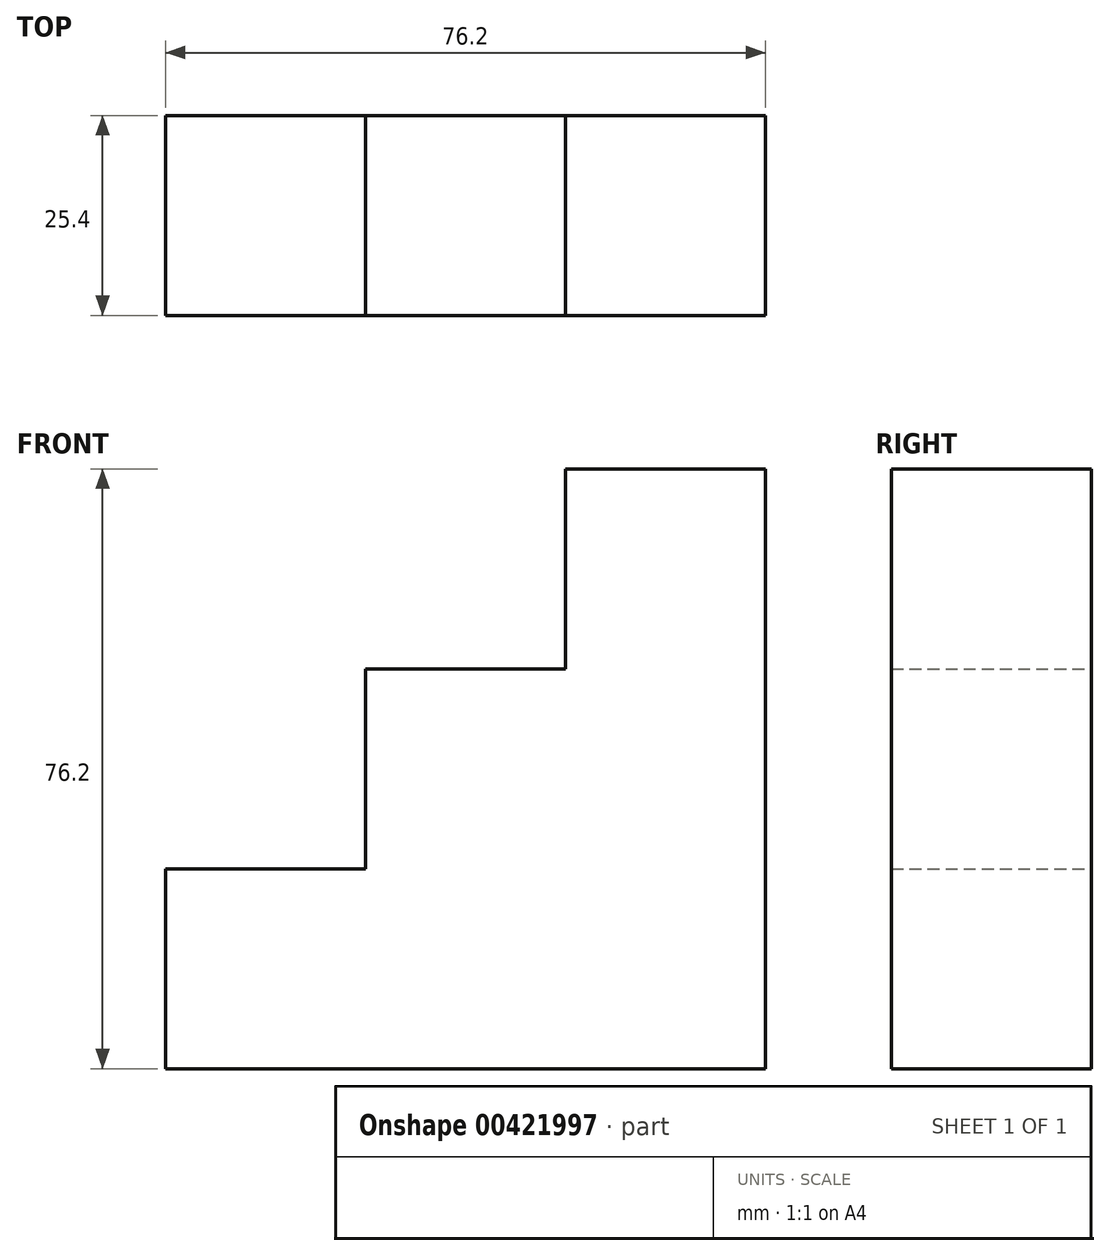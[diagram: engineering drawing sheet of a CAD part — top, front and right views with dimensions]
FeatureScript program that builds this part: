
annotation { "Feature Type Name" : "Feature", "Feature Type Description" : "" }
export const myFeature = defineFeature(function(context is Context, id is Id, definition is map)
    precondition{}
    {
        {
            var Q0;
            Q0=qCreatedBy(makeId("Front.planeOp"),FACE);
            var sketch = newSketch(context, id + "F0", { "sketchPlane" : qUnion([Q0])});
            skLineSegment(sketch, "E0", {"start": v(0, 0) * mm, "end": v(-76.2, 0) * mm});
            skLineSegment(sketch, "E1", {"start": v(-76.2, 0) * mm, "end": v(-76.2, 25.4) * mm});
            skLineSegment(sketch, "E2", {"start": v(-76.2, 25.4) * mm, "end": v(-50.8, 25.4) * mm});
            skLineSegment(sketch, "E3", {"start": v(-50.8, 25.4) * mm, "end": v(-50.8, 50.8) * mm});
            skLineSegment(sketch, "E4", {"start": v(-50.8, 50.8) * mm, "end": v(-25.4, 50.8) * mm});
            skLineSegment(sketch, "E5", {"start": v(-25.4, 50.8) * mm, "end": v(-25.4, 76.2) * mm});
            skLineSegment(sketch, "E6", {"start": v(-25.4, 76.2) * mm, "end": v(0, 76.2) * mm});
            skLineSegment(sketch, "E7", {"start": v(0, 0) * mm, "end": v(0, 76.2) * mm});
            skSolve(sketch);
        }
        {
            var Q0;
            Q0 = qSketchRegion(id + "F0", true);
            extrude(context, id + "F1", {"entities" : qUnion([Q0]), "depth" : 25.4 * mm});
        }
    });
